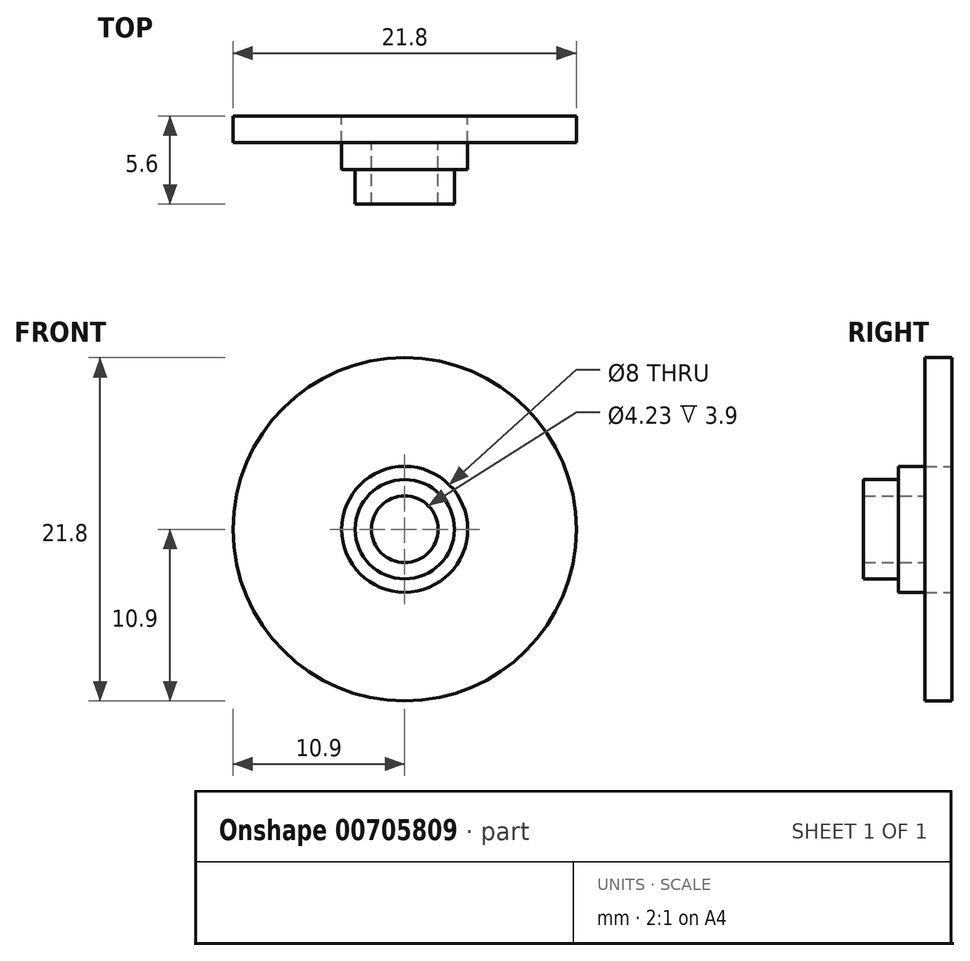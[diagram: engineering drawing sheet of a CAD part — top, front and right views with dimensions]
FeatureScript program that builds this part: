
annotation { "Feature Type Name" : "Feature", "Feature Type Description" : "" }
export const myFeature = defineFeature(function(context is Context, id is Id, definition is map)
    precondition{}
    {
        {
            var Q0;
            Q0=qCreatedBy(makeId("Front.planeOp"),FACE);
            var sketch = newSketch(context, id + "F0", { "sketchPlane" : qUnion([Q0])});
            skCircle(sketch, "E0", {"center": v(0, 0) * mm, "radius": 10.9 * mm});
            skCircle(sketch, "E1", {"center": v(0, 0) * mm, "radius": 4 * mm});
            skCircle(sketch, "E2", {"center": v(0, 0) * mm, "radius": 3.15 * mm});
            skCircle(sketch, "E3", {"center": v(0, 0) * mm, "radius": 2.12 * mm});
            skSolve(sketch);
        }
        {
            var Q0;
            Q0=makeQuery(id+"F0.imprint","IMPRINT",FACE,{"disambiguationData":[TD([[makeQuery(id+"F0.imprint","IMPRINT",EDGE,{"derivedFrom":sQuery(id+"F0.wireOp",EDGE,"E0")}),1.0]])]});
            var Q1;
            Q1=makeQuery(id+"F0.imprint","IMPRINT",FACE,{"disambiguationData":[TD([[makeQuery(id+"F0.imprint","IMPRINT",EDGE,{"derivedFrom":sQuery(id+"F0.wireOp",EDGE,"E3")}),1.0]])]});
            extrude(context, id + "F1", {"entities" : qUnion([Q0, Q1]), "depth" : 1.7 * mm, "offsetDistance" : 25 * mm});
        }
        {
            var Q0;
            Q0=makeQuery(id+"F0.imprint","IMPRINT",FACE,{"disambiguationData":[TD([[makeQuery(id+"F0.imprint","IMPRINT",EDGE,{"derivedFrom":sQuery(id+"F0.wireOp",EDGE,"E1")}),1.0]])]});
            extrude(context, id + "F2", {"entities" : qUnion([Q0]), "depth" : 3.4 * mm, "offsetDistance" : 25 * mm});
        }
        {
            var Q0;
            Q0=makeQuery(id+"F0.imprint","IMPRINT",FACE,{"disambiguationData":[TD([[makeQuery(id+"F0.imprint","IMPRINT",EDGE,{"derivedFrom":sQuery(id+"F0.wireOp",EDGE,"E2")}),1.0]])]});
            extrude(context, id + "F3", {"entities" : qUnion([Q0]), "operationType" : NewBodyOperationType.ADD, "depth" : 5.6 * mm, "offsetDistance" : 25 * mm});
        }
    });
